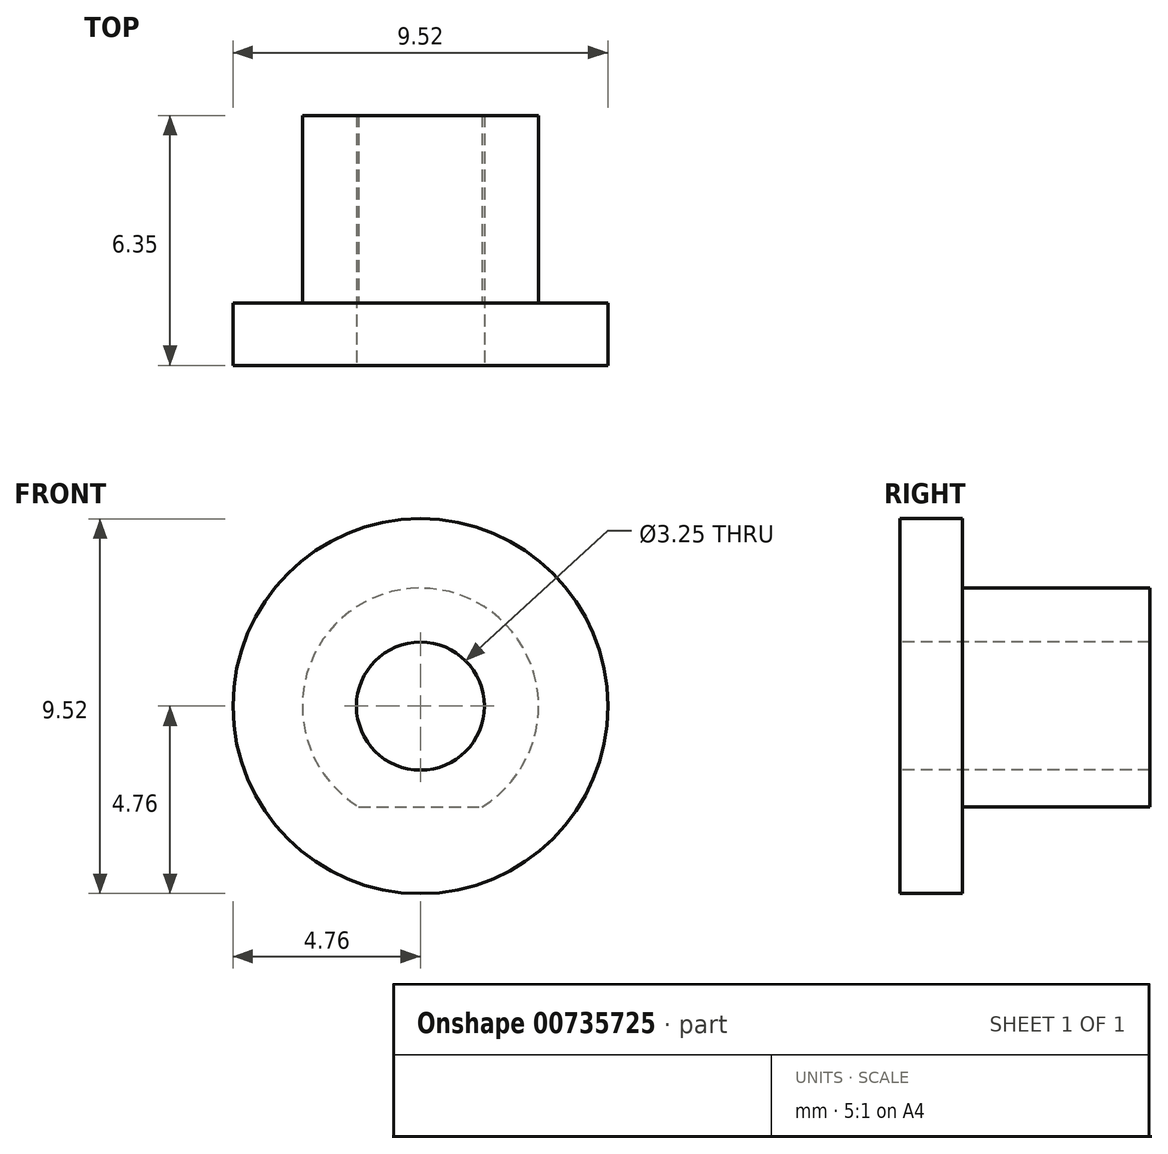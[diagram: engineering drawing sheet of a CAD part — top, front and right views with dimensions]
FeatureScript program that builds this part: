
annotation { "Feature Type Name" : "Feature", "Feature Type Description" : "" }
export const myFeature = defineFeature(function(context is Context, id is Id, definition is map)
    precondition{}
    {
        {
            var Q0;
            Q0=qCreatedBy(makeId("Front.planeOp"),FACE);
            var sketch = newSketch(context, id + "F0", { "sketchPlane" : qUnion([Q0])});
            skCircle(sketch, "E0", {"center": v(0, 0) * mm, "radius": 4.76 * mm});
            skCircle(sketch, "E1", {"center": v(0, 0) * mm, "radius": 3 * mm});
            skCircle(sketch, "E2", {"center": v(0, 0) * mm, "radius": 1.63 * mm});
            skLineSegment(sketch, "E3", {"start": v(0, -2.56) * mm, "end": v(-1.57, -2.56) * mm});
            skLineSegment(sketch, "E4", {"start": v(-1.57, -2.56) * mm, "end": v(1.57, -2.56) * mm});
            skSolve(sketch);
        }
        {
            var Q0;
            Q0=makeQuery(id+"F0.imprint","IMPRINT",FACE,{"disambiguationData":[TD([[makeQuery(id+"F0.imprint","IMPRINT",EDGE,{"derivedFrom":sQuery(id+"F0.wireOp",EDGE,"E0")}),1.0]])]});
            var Q1;
            {var subQ0=sQuery(id+"F0.wireOp",EDGE,"E4");var subQ4=makeQuery(id+"F0.imprint","IMPRINT",VERTEX,{"derivedFrom":subQ0});Q1=makeQuery(id+"F0.imprint","IMPRINT",FACE,{"disambiguationData":[TD([[makeQuery(id+"F0.imprint","IMPRINT",EDGE,{"disambiguationData":[TD([[subQ4,1.0]])],"derivedFrom":subQ0}),-1.0]])]});}
            extrude(context, id + "F1", {"entities" : qUnion([Q0, Q1]), "oppositeDirection" : true, "depth" : 1.59 * mm, "offsetDistance" : 25.4 * mm});
        }
        {
            var Q0;
            Q0=makeQuery(id+"F0.imprint","IMPRINT",FACE,{"disambiguationData":[TD([[makeQuery(id+"F0.imprint","IMPRINT",EDGE,{"derivedFrom":sQuery(id+"F0.wireOp",EDGE,"E2")}),-1.0]])]});
            extrude(context, id + "F2", {"entities" : qUnion([Q0]), "operationType" : NewBodyOperationType.ADD, "oppositeDirection" : true, "depth" : 6.35 * mm, "offsetDistance" : 25.4 * mm});
        }
    });
